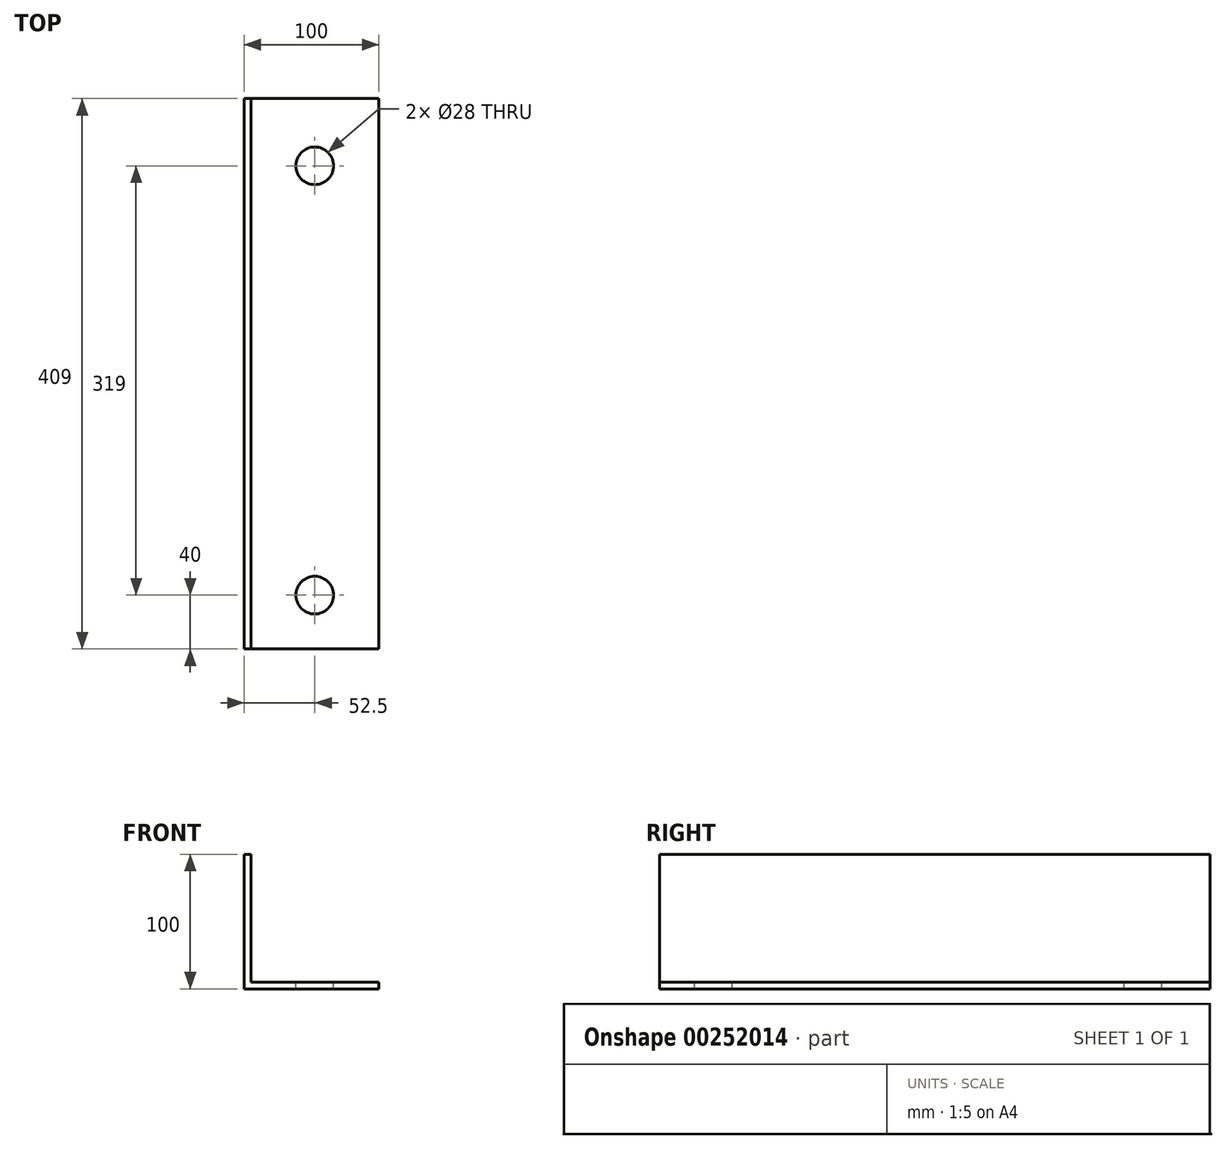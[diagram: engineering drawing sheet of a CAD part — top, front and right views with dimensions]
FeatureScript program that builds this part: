
annotation { "Feature Type Name" : "Feature", "Feature Type Description" : "" }
export const myFeature = defineFeature(function(context is Context, id is Id, definition is map)
    precondition{}
    {
        {
            var Q0;
            Q0=qCreatedBy(makeId("Front.planeOp"),FACE);
            var sketch = newSketch(context, id + "F0", { "sketchPlane" : qUnion([Q0])});
            skLineSegment(sketch, "E0", {"start": v(0, 100) * mm, "end": v(0, 0) * mm});
            skLineSegment(sketch, "E1", {"start": v(0, 0) * mm, "end": v(100, 0) * mm});
            skLineSegment(sketch, "E2", {"start": v(0, 100) * mm, "end": v(5, 100) * mm});
            skLineSegment(sketch, "E3", {"start": v(5, 100) * mm, "end": v(5, 5) * mm});
            skLineSegment(sketch, "E4", {"start": v(5, 5) * mm, "end": v(100, 5) * mm});
            skLineSegment(sketch, "E5", {"start": v(100, 5) * mm, "end": v(100, 0) * mm});
            skSolve(sketch);
        }
        {
            var Q0;
            Q0=makeQuery(id+"F0.imprint","IMPRINT",FACE,{"disambiguationData":[TD([[makeQuery(id+"F0.imprint","IMPRINT",EDGE,{"derivedFrom":sQuery(id+"F0.wireOp",EDGE,"E0")}),1.0]])]});
            extrude(context, id + "F1", {"entities" : qUnion([Q0]), "depth" : 409 * mm});
        }
        {
            var Q0;
            Q0=makeQuery(id+"F1.opExtrude","SWEPT_FACE",FACE,{"disambiguationData":[OSD([sQuery(id+"F0.wireOp",EDGE,"E4")])]});
            var sketch = newSketch(context, id + "F2", { "sketchPlane" : qUnion([Q0])});
            skCircle(sketch, "E6", {"center": v(52.5, -50) * mm, "radius": 14 * mm});
            skCircle(sketch, "E7", {"center": v(52.5, -369) * mm, "radius": 14 * mm});
            skSolve(sketch);
        }
        {
            var Q0;
            Q0=makeQuery(id+"F2.imprint","IMPRINT",FACE,{"disambiguationData":[TD([[makeQuery(id+"F2.imprint","IMPRINT",EDGE,{"derivedFrom":sQuery(id+"F2.wireOp",EDGE,"E6")}),1.0]])]});
            var Q1;
            Q1=makeQuery(id+"F2.imprint","IMPRINT",FACE,{"disambiguationData":[TD([[makeQuery(id+"F2.imprint","IMPRINT",EDGE,{"derivedFrom":sQuery(id+"F2.wireOp",EDGE,"E7")}),1.0]])]});
            var Q2;
            Q2=makeQuery(id+"F1.opExtrude","SWEPT_FACE",FACE,{"disambiguationData":[OSD([sQuery(id+"F0.wireOp",EDGE,"E1")])]});
            extrude(context, id + "F3", {"entities" : qUnion([Q0, Q1]), "operationType" : NewBodyOperationType.REMOVE, "endBound" : BoundingType.UP_TO_SURFACE, "oppositeDirection" : true, "endBoundEntityFace" : qUnion([Q2]), "depth" : 25 * mm});
        }
    });
